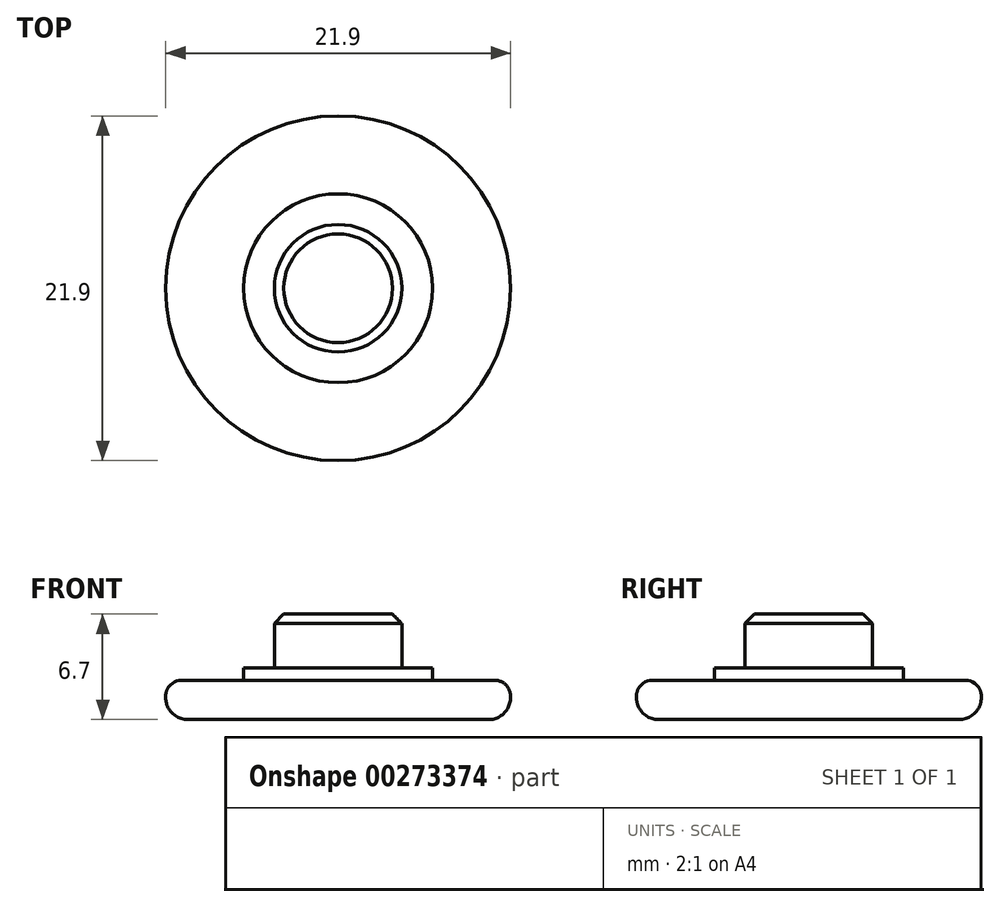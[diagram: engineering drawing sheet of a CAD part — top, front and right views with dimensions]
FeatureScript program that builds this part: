
annotation { "Feature Type Name" : "Feature", "Feature Type Description" : "" }
export const myFeature = defineFeature(function(context is Context, id is Id, definition is map)
    precondition{}
    {
        {
            var Q0;
            Q0=qCreatedBy(makeId("Top.planeOp"),FACE);
            var sketch = newSketch(context, id + "F0", { "sketchPlane" : qUnion([Q0])});
            skCircle(sketch, "E0", {"center": v(0, 0) * mm, "radius": 10.95 * mm});
            skSolve(sketch);
        }
        {
            var Q0;
            Q0=makeQuery(id+"F0.imprint","IMPRINT",FACE,{"disambiguationData":[TD([[makeQuery(id+"F0.imprint","IMPRINT",EDGE,{"derivedFrom":sQuery(id+"F0.wireOp",EDGE,"E0")}),1.0]])]});
            extrude(context, id + "F1", {"entities" : qUnion([Q0]), "depth" : 2.5 * mm});
        }
        {
            var Q0;
            Q0=makeQuery(id+"F1.opExtrude","CAP_FACE",FACE,{"disambiguationData":[OSD([sQuery(id+"F0.wireOp",EDGE,"E0")])],"isStart":false});
            var sketch = newSketch(context, id + "F2", { "sketchPlane" : qUnion([Q0])});
            skCircle(sketch, "E1", {"center": v(0, 0) * mm, "radius": 4.05 * mm});
            skSolve(sketch);
        }
        {
            var Q0;
            Q0=makeQuery(id+"F2.imprint","IMPRINT",FACE,{"disambiguationData":[TD([[makeQuery(id+"F2.imprint","IMPRINT",EDGE,{"derivedFrom":sQuery(id+"F2.wireOp",EDGE,"E1")}),1.0]])]});
            extrude(context, id + "F3", {"entities" : qUnion([Q0]), "operationType" : NewBodyOperationType.ADD, "depth" : 4.2 * mm});
        }
        {
            var Q0;
            Q0=makeQuery(id+"F1.opExtrude","CAP_EDGE",EDGE,{"disambiguationData":[OSD([sQuery(id+"F0.wireOp",EDGE,"E0")])],"isStart":false});
            fillet(context, id + "F4", {"entities" : qUnion([Q0]), "radius" : 1 * mm, "tangentPropagation" : true, "allowEdgeOverflow" : false});
        }
        {
            var Q0;
            Q0=makeQuery(id+"F1.opExtrude","CAP_FACE",FACE,{"disambiguationData":[OSD([sQuery(id+"F0.wireOp",EDGE,"E0")])],"isStart":false});
            var sketch = newSketch(context, id + "F5", { "sketchPlane" : qUnion([Q0])});
            skCircle(sketch, "E2", {"center": v(0, 0) * mm, "radius": 6 * mm});
            skSolve(sketch);
        }
        {
            var Q0;
            Q0=makeQuery(id+"F5.imprint","IMPRINT",FACE,{"disambiguationData":[TD([[makeQuery(id+"F5.imprint","IMPRINT",EDGE,{"derivedFrom":sQuery(id+"F5.wireOp",EDGE,"E2")}),1.0]])]});
            extrude(context, id + "F6", {"entities" : qUnion([Q0]), "operationType" : NewBodyOperationType.ADD, "depth" : .8 * mm});
        }
        {
            var Q0;
            Q0=makeQuery(id+"F1.opExtrude","CAP_EDGE",EDGE,{"disambiguationData":[OSD([sQuery(id+"F0.wireOp",EDGE,"E0")])],"isStart":true});
            fillet(context, id + "F7", {"entities" : qUnion([Q0]), "radius" : 1.4 * mm, "tangentPropagation" : true, "allowEdgeOverflow" : false});
        }
        {
            var Q0;
            Q0=makeQuery(id+"F3.opExtrude","CAP_EDGE",EDGE,{"disambiguationData":[OSD([sQuery(id+"F2.wireOp",EDGE,"E1")])],"isStart":false});
            chamfer(context, id + "F8", {"entities" : qUnion([Q0]), "width" : .6 * mm, "tangentPropagation" : true});
        }
    });
